# Revit family: Desk-Teknion-JNWDSN-Double_Sided_Rectangular-R2018
name_source: partatom
category: Furniture
revit_build: Autodesk Revit 2018 (Build: 20190510_1515(x64)
units: mm (PartAtom-declared; Revit-internal decimal feet)

## family parameters
Always vertical = Yes
Cut with Voids When Loaded = No
OmniClass Number = 23.40.20.00
OmniClass Title = General Furniture and Specialties
Room Calculation Point = No
Shared = Yes
Work Plane-Based = No

## types (3) — shared parameters
Assembly Code = E2020200
Description = Double-Sided Rectangular Worksurface
Manufacturer = Teknion
Manufacturer Fax = 416.661.4586
Part Number = JNWDSN
Product Documentation Link = http://www.teknion.com
Product Line = Expansion Cityline
Product Page URL = http://www.teknion.com
Series = Expansion Cityline
Sustainability Data = http://www.teknion.com
URL = www.teknion.com
Unit Weight URL = http://www.teknion.com
Warranty = http://www.teknion.com

## per-type parameters (varying)
| type | Depth | Model |
| 36" Depth | 36 " | JNWDSN36 |
| 48" Depth | 48 " | JNWDSN48 |
| 60" Depth | 60 " | JNWDSN60 |

## geometry (parser evidence)
native form markers: Sweep x2
no freeform markers — native parametric forms only
